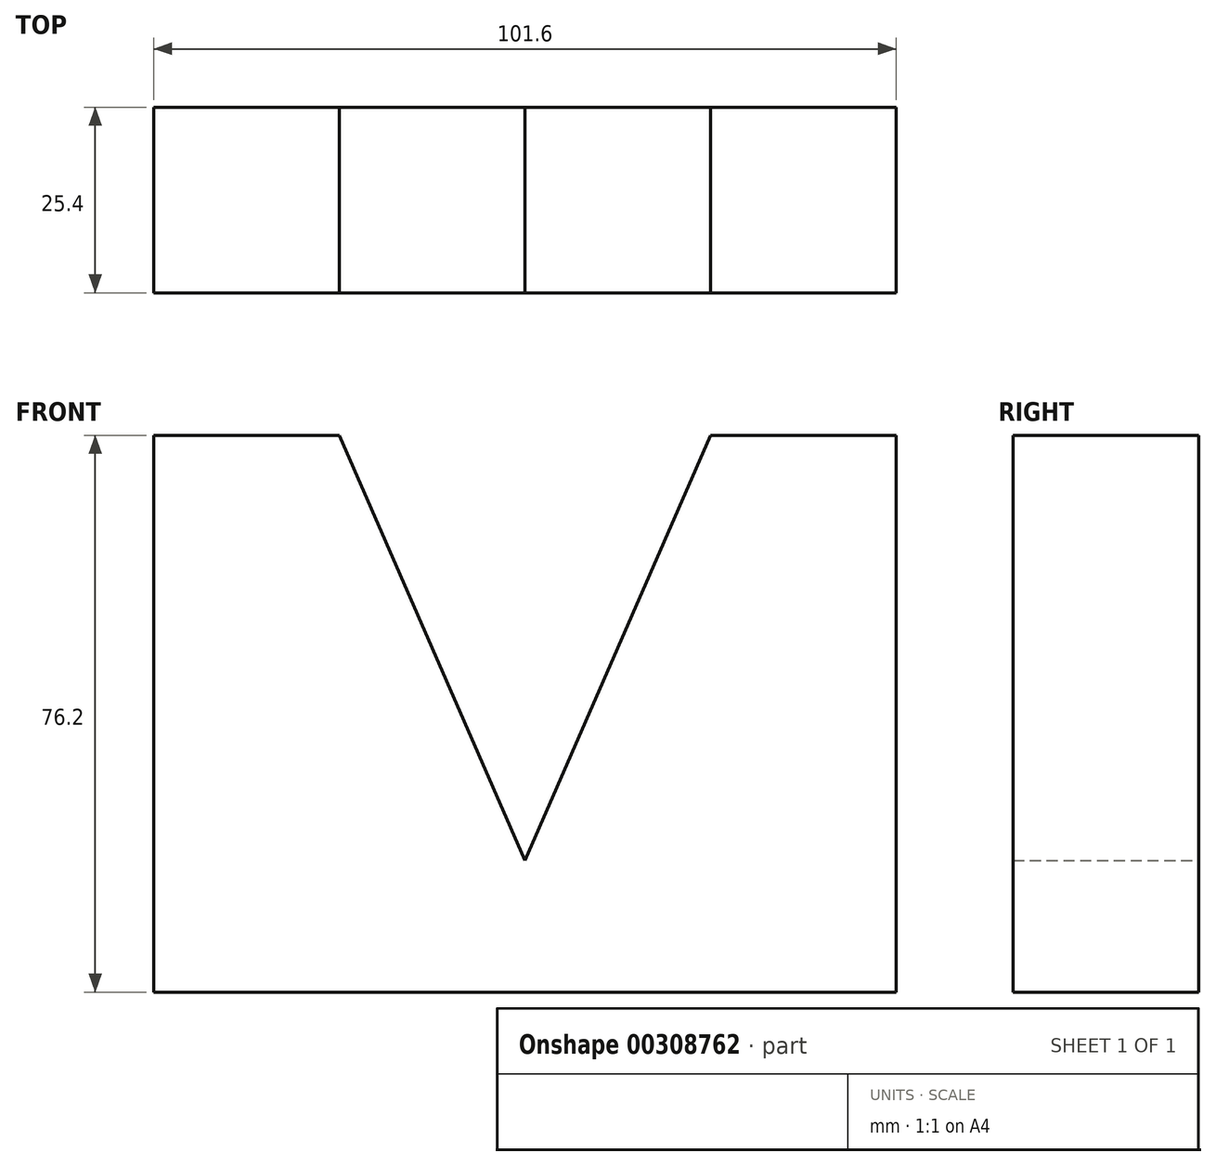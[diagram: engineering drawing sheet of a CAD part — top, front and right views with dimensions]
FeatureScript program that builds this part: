
annotation { "Feature Type Name" : "Feature", "Feature Type Description" : "" }
export const myFeature = defineFeature(function(context is Context, id is Id, definition is map)
    precondition{}
    {
        {
            var Q0;
            Q0=qCreatedBy(makeId("Front.planeOp"),FACE);
            var sketch = newSketch(context, id + "F0", { "sketchPlane" : qUnion([Q0])});
            skLineSegment(sketch, "E0", {"start": v(-34.06, -78.42) * mm, "end": v(67.54, -78.42) * mm});
            skLineSegment(sketch, "E1", {"start": v(67.54, -78.42) * mm, "end": v(67.54, -2.22) * mm});
            skLineSegment(sketch, "E2", {"start": v(67.54, -2.22) * mm, "end": v(42.14, -2.22) * mm});
            skLineSegment(sketch, "E3", {"start": v(42.14, -2.22) * mm, "end": v(16.74, -60.42) * mm});
            skLineSegment(sketch, "E4", {"start": v(16.74, -60.42) * mm, "end": v(-8.66, -2.22) * mm});
            skLineSegment(sketch, "E5", {"start": v(-8.66, -2.22) * mm, "end": v(-34.06, -2.22) * mm});
            skLineSegment(sketch, "E6", {"start": v(-34.06, -2.22) * mm, "end": v(-34.06, -78.42) * mm});
            skSolve(sketch);
        }
        {
            var Q0;
            Q0=makeQuery(id+"F0.imprint","IMPRINT",FACE,{"disambiguationData":[TD([[makeQuery(id+"F0.imprint","IMPRINT",EDGE,{"derivedFrom":sQuery(id+"F0.wireOp",EDGE,"E0")}),1.0]])]});
            extrude(context, id + "F1", {"entities" : qUnion([Q0]), "depth" : 25.4 * mm});
        }
    });
